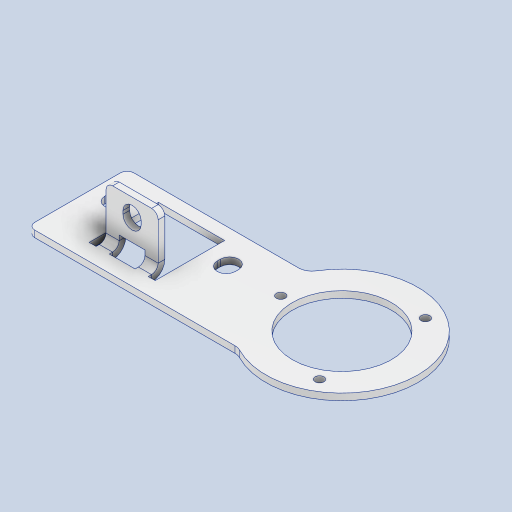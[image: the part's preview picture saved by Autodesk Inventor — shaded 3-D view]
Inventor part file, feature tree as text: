
AUTODESK INVENTOR PART (.ipt)
format: ipt  version: 2023 (Build 270158000, 158)  size: 324,096 bytes
history: native  units: mm
features: other x7, fillet x3, sketch x3, hole x1
ambient origin geometry x8: Origin, YZ Plane, XZ Plane, XY Plane, X Axis, Y Axis, Z Axis, Center Point
bodies: Body1 (feature_tree), Body2 (feature_tree)
feature tree (14):
  other  "GIM3505-8_with-driver.ipt"
  other  "折り曲げ3"
  fillet  "フィレット1"  Radius=10.0mm
  fillet  "フィレット2"  Radius=46.0mm
  fillet  "フィレット3"  Radius=30.0mm
  hole  "穴1"  [1 undecoded]
  other  "TaggingFeature1"
  sketch  "スケッチ1"
  other  "プレート2"
  sketch  "スケッチ6"
  sketch  "スケッチ7"
  other  "ソリッド1::GIM3505-8_with-driver.ipt"
  other  "Srf1"
  other  "ソリッド1"
note: 1 required parameter value undecoded (feature->parameter linkage not recoverable at this tier; creation-order binding heuristic only, values carry confidence <= 0.55)
